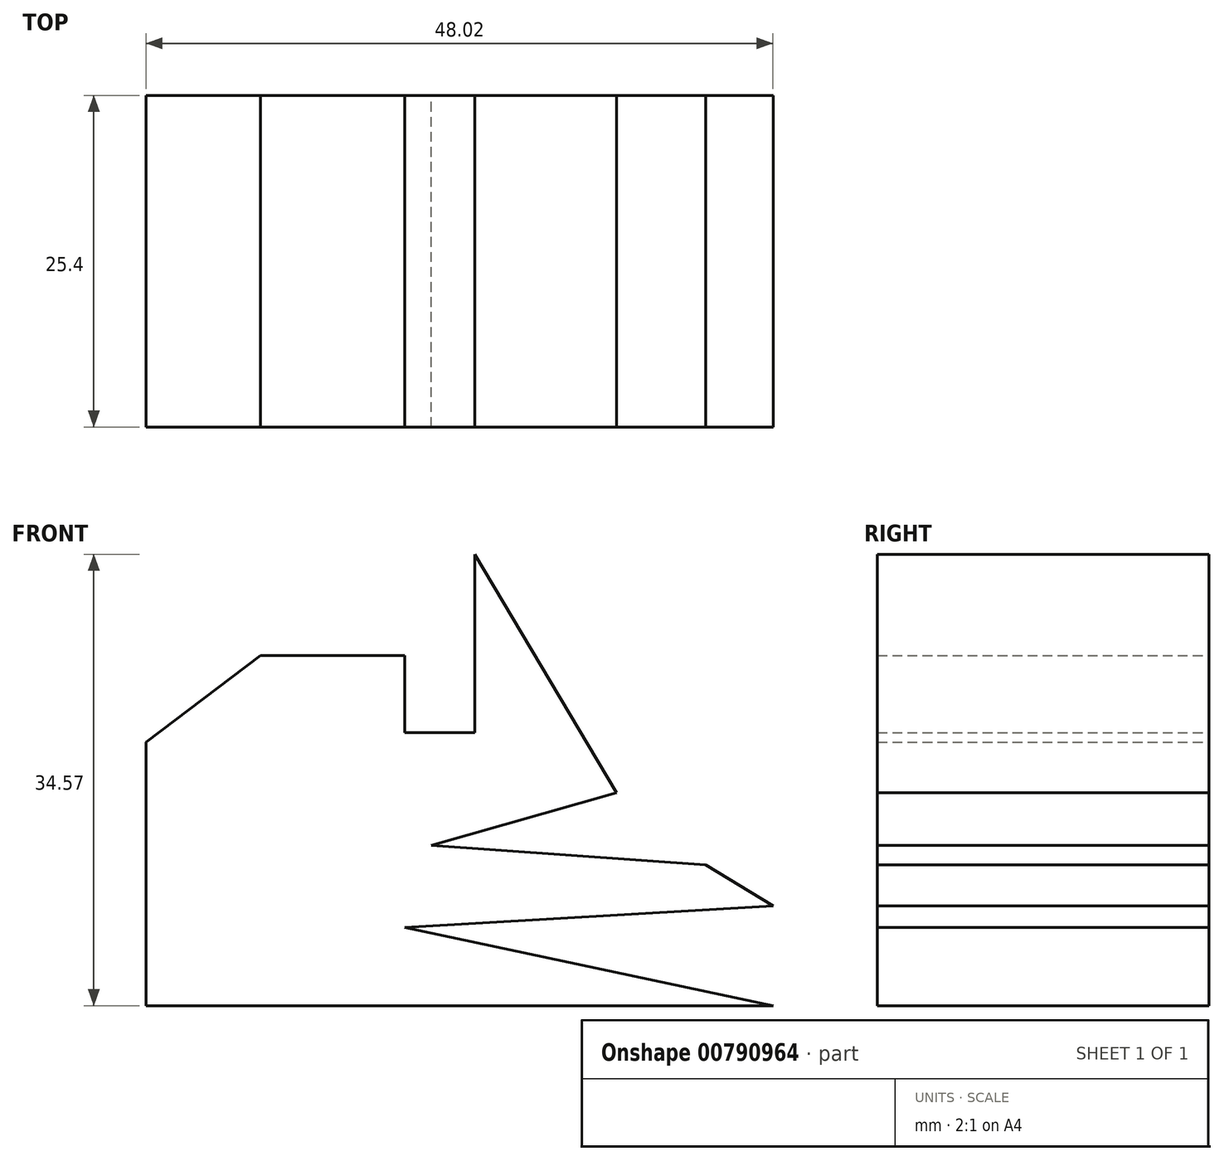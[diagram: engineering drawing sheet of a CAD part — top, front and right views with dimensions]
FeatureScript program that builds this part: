
annotation { "Feature Type Name" : "Feature", "Feature Type Description" : "" }
export const myFeature = defineFeature(function(context is Context, id is Id, definition is map)
    precondition{}
    {
        {
            var Q0;
            Q0=qCreatedBy(makeId("Front.planeOp"),FACE);
            var sketch = newSketch(context, id + "F0", { "sketchPlane" : qUnion([Q0])});
            skLineSegment(sketch, "E0", {"start": v(0, 0) * mm, "end": v(0, 20.19) * mm});
            skLineSegment(sketch, "E1", {"start": v(0, 20.19) * mm, "end": v(8.76, 26.82) * mm});
            skLineSegment(sketch, "E2", {"start": v(8.76, 26.82) * mm, "end": v(19.82, 26.82) * mm});
            skLineSegment(sketch, "E3", {"start": v(19.82, 26.82) * mm, "end": v(19.82, 20.92) * mm});
            skLineSegment(sketch, "E4", {"start": v(19.82, 20.92) * mm, "end": v(25.16, 20.92) * mm});
            skLineSegment(sketch, "E5", {"start": v(25.16, 20.92) * mm, "end": v(25.16, 34.57) * mm});
            skLineSegment(sketch, "E6", {"start": v(25.16, 34.57) * mm, "end": v(36.04, 16.32) * mm});
            skLineSegment(sketch, "E7", {"start": v(36.04, 16.32) * mm, "end": v(21.85, 12.26) * mm});
            skLineSegment(sketch, "E8", {"start": v(21.85, 12.26) * mm, "end": v(42.86, 10.78) * mm});
            skLineSegment(sketch, "E9", {"start": v(42.86, 10.78) * mm, "end": v(48.02, 7.65) * mm});
            skLineSegment(sketch, "E10", {"start": v(48.02, 7.65) * mm, "end": v(19.82, 6) * mm});
            skLineSegment(sketch, "E11", {"start": v(19.82, 6) * mm, "end": v(48.02, 0) * mm});
            skLineSegment(sketch, "E12", {"start": v(48.02, 0) * mm, "end": v(0, 0) * mm});
            skSolve(sketch);
        }
        {
            var Q0;
            Q0=makeQuery(id+"F0.imprint","IMPRINT",FACE,{"disambiguationData":[TD([[makeQuery(id+"F0.imprint","IMPRINT",EDGE,{"derivedFrom":sQuery(id+"F0.wireOp",EDGE,"E0")}),-1.0]])]});
            extrude(context, id + "F1", {"entities" : qUnion([Q0]), "depth" : 25.4 * mm, "offsetDistance" : 25.4 * mm});
        }
    });
